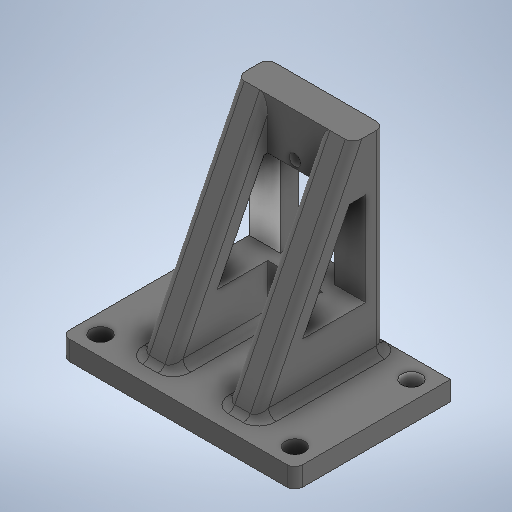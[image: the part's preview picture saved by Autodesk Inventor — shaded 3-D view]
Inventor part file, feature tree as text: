
AUTODESK INVENTOR PART (.ipt)
format: ipt  version: 2025.2 (Build 292293000, 293)  size: 445,440 bytes
history: native  units: mm
features: sketch x16, extrude x8, hole x4, fillet x3, other x1
ambient origin geometry x8: Origin, YZ Plane, XZ Plane, XY Plane, X Axis, Y Axis, Z Axis, Center Point
bodies: Body1 (feature_tree)
feature tree (32):
  other  "Bryła1"
  extrude  "Wyciągnięcie proste1"  Depth=60.0mm
  hole  "Otwór1"  [1 undecoded]
  fillet  "Zaokrąglenie1"  Radius=5.0mm
  extrude  "Wyciągnięcie proste2"  Depth=2.0mm
  sketch  "Szkic8"
  extrude  "Wyciągnięcie proste3"  Depth=7.0mm
  sketch  "Szkic10"
  hole  "Otwór2"  [1 undecoded]
  hole  "Otwór3"  [1 undecoded]
  extrude  "Wyciągnięcie proste4"  Depth=25.0mm
  extrude  "Wyciągnięcie proste5"  Depth=8.0mm
  fillet  "Zaokrąglenie2"  Radius=25.0mm
  sketch  "Szkic15"
  extrude  "Wyciągnięcie proste6"  Depth=30.0mm
  fillet  "Zaokrąglenie3"  Radius=8.0mm
  extrude  "Wyciągnięcie proste7"  Depth=50.0mm TaperAngle=0.0deg
  sketch  "Szkic18"
  extrude  "Wyciągnięcie proste8"  Depth=13.0mm
  hole  "Otwór4"  [1 undecoded]
  sketch  "Szkic1"
  sketch  "Szkic2"
  sketch  "Szkic5"
  sketch  "Szkic9"
  sketch  "Szkic11"
  sketch  "Szkic12"
  sketch  "Szkic13"
  sketch  "Szkic14"
  sketch  "Szkic16"
  sketch  "Szkic17"
  sketch  "Szkic19"
  sketch  "Szkic20"
note: 4 required parameter values undecoded (feature->parameter linkage not recoverable at this tier; creation-order binding heuristic only, values carry confidence <= 0.55)
